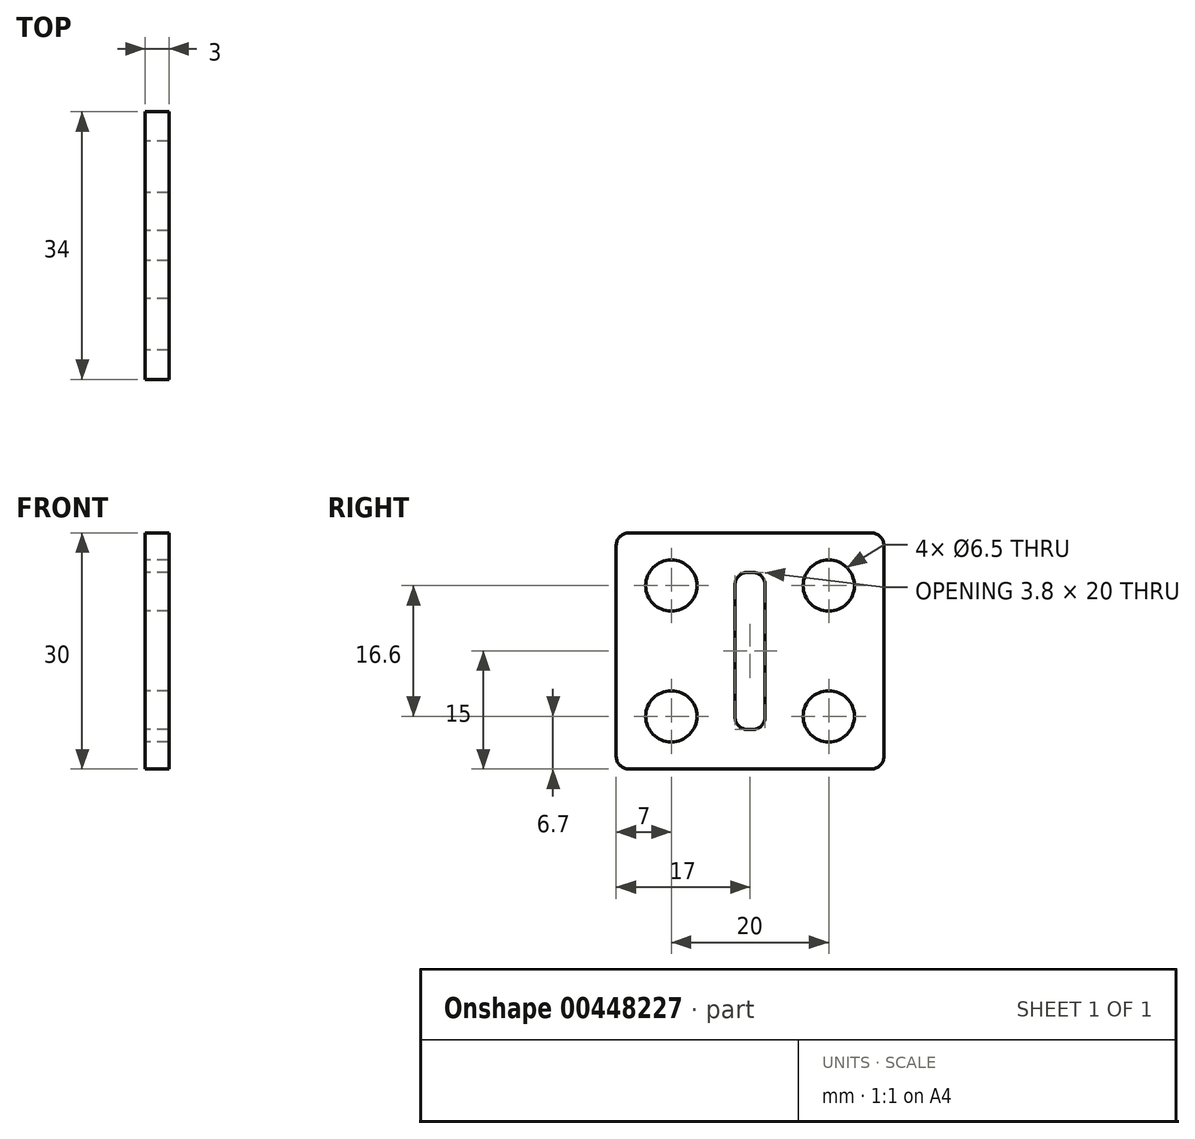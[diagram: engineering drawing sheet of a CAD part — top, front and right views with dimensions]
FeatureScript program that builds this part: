
annotation { "Feature Type Name" : "Feature", "Feature Type Description" : "" }
export const myFeature = defineFeature(function(context is Context, id is Id, definition is map)
    precondition{}
    {
        {
            var Q0;
            Q0=qCreatedBy(makeId("Right.planeOp"),FACE);
            var sketch = newSketch(context, id + "F0", { "sketchPlane" : qUnion([Q0])});
            skLineSegment(sketch, "E0.bottom", {"start": v(17, -15) * mm, "end": v(-17, -15) * mm});
            skLineSegment(sketch, "E0.top", {"start": v(17, 15) * mm, "end": v(-17, 15) * mm});
            skLineSegment(sketch, "E0.left", {"start": v(17, -15) * mm, "end": v(17, 15) * mm});
            skLineSegment(sketch, "E0.right", {"start": v(-17, -15) * mm, "end": v(-17, 15) * mm});
            skPoint(sketch, "E0.middle", {"position": v(0, 0) * mm});
            skLineSegment(sketch, "E1.bottom", {"start": v(1.9, -10) * mm, "end": v(-1.9, -10) * mm});
            skLineSegment(sketch, "E1.top", {"start": v(1.9, 10) * mm, "end": v(-1.9, 10) * mm});
            skLineSegment(sketch, "E1.left", {"start": v(1.9, -10) * mm, "end": v(1.9, 10) * mm});
            skLineSegment(sketch, "E1.right", {"start": v(-1.9, -10) * mm, "end": v(-1.9, 10) * mm});
            skLineSegment(sketch, "E2", {"start": v(10, 15) * mm, "end": v(10, -15) * mm, "construction": true});
            skLineSegment(sketch, "E3", {"start": v(-10, 15) * mm, "end": v(-10, -15) * mm, "construction": true});
            skLineSegment(sketch, "E4", {"start": v(17, 8.3) * mm, "end": v(-17, 8.3) * mm, "construction": true});
            skLineSegment(sketch, "E5", {"start": v(17, -8.3) * mm, "end": v(-17, -8.3) * mm, "construction": true});
            skPoint(sketch, "E6", {"position": v(10, 8.3) * mm});
            skPoint(sketch, "E7", {"position": v(-10, 8.3) * mm});
            skPoint(sketch, "E8", {"position": v(-10, -8.3) * mm});
            skPoint(sketch, "E9", {"position": v(10, -8.3) * mm});
            skSolve(sketch);
        }
        {
            var Q0;
            Q0=makeQuery(id+"F0.imprint","IMPRINT",FACE,{"disambiguationData":[TD([[makeQuery(id+"F0.imprint","IMPRINT",EDGE,{"derivedFrom":sQuery(id+"F0.wireOp",EDGE,"E0.bottom")}),-1.0]])]});
            extrude(context, id + "F1", {"entities" : qUnion([Q0]), "depth" : 3 * mm, "offsetDistance" : 25 * mm});
        }
        {
            var Q0;
            Q0=makeQuery(id+"F1.opExtrude","SWEPT_EDGE",EDGE,{"disambiguationData":[OSD([sQuery(id+"F0.wireOp",EDGE,"AEXB3O9J-t11H-Sehj-6pxe-2tEOLs6rYygq.top"),sQuery(id+"F0.wireOp",EDGE,"AEXB3O9J-t11H-Sehj-6pxe-2tEOLs6rYygq.right")])]});
            var Q1;
            Q1=makeQuery(id+"F1.opExtrude","SWEPT_EDGE",EDGE,{"disambiguationData":[OSD([sQuery(id+"F0.wireOp",EDGE,"AEXB3O9J-t11H-Sehj-6pxe-2tEOLs6rYygq.top"),sQuery(id+"F0.wireOp",EDGE,"AEXB3O9J-t11H-Sehj-6pxe-2tEOLs6rYygq.left")])]});
            var Q2;
            Q2=makeQuery(id+"F1.opExtrude","SWEPT_EDGE",EDGE,{"disambiguationData":[OSD([sQuery(id+"F0.wireOp",EDGE,"E1.top"),sQuery(id+"F0.wireOp",EDGE,"E1.right")])]});
            var Q3;
            Q3=makeQuery(id+"F1.opExtrude","SWEPT_EDGE",EDGE,{"disambiguationData":[OSD([sQuery(id+"F0.wireOp",EDGE,"E1.top"),sQuery(id+"F0.wireOp",EDGE,"E1.left")])]});
            var Q4;
            Q4=makeQuery(id+"F1.opExtrude","SWEPT_EDGE",EDGE,{"disambiguationData":[OSD([sQuery(id+"F0.wireOp",EDGE,"1eccf574-d479-46f1-8f8d-4602f6f3811f2.MirrorCS"),sQuery(id+"F0.wireOp",EDGE,"1eccf574-d479-46f1-8f8d-4602f6f3811f3.MirrorCS")])]});
            var Q5;
            Q5=makeQuery(id+"F1.opExtrude","SWEPT_EDGE",EDGE,{"disambiguationData":[OSD([sQuery(id+"F0.wireOp",EDGE,"1eccf574-d479-46f1-8f8d-4602f6f3811f1.MirrorCS"),sQuery(id+"F0.wireOp",EDGE,"1eccf574-d479-46f1-8f8d-4602f6f3811f3.MirrorCS")])]});
            var Q6;
            Q6=makeQuery(id+"F1.opExtrude","SWEPT_EDGE",EDGE,{"disambiguationData":[OSD([sQuery(id+"F0.wireOp",EDGE,"AEXB3O9J-t11H-Sehj-6pxe-2tEOLs6rYygq.bottom"),sQuery(id+"F0.wireOp",EDGE,"AEXB3O9J-t11H-Sehj-6pxe-2tEOLs6rYygq.right")])]});
            var Q7;
            Q7=makeQuery(id+"F1.opExtrude","SWEPT_EDGE",EDGE,{"disambiguationData":[OSD([sQuery(id+"F0.wireOp",EDGE,"AEXB3O9J-t11H-Sehj-6pxe-2tEOLs6rYygq.bottom"),sQuery(id+"F0.wireOp",EDGE,"AEXB3O9J-t11H-Sehj-6pxe-2tEOLs6rYygq.left")])]});
            var Q8;
            Q8=makeQuery(id+"F1.opExtrude","SWEPT_EDGE",EDGE,{"disambiguationData":[OSD([sQuery(id+"F0.wireOp",EDGE,"E1.bottom"),sQuery(id+"F0.wireOp",EDGE,"E1.right")])]});
            var Q9;
            Q9=makeQuery(id+"F1.opExtrude","SWEPT_EDGE",EDGE,{"disambiguationData":[OSD([sQuery(id+"F0.wireOp",EDGE,"E1.bottom"),sQuery(id+"F0.wireOp",EDGE,"E1.left")])]});
            var Q10;
            Q10=makeQuery(id+"F1.opExtrude","SWEPT_EDGE",EDGE,{"disambiguationData":[OSD([sQuery(id+"F0.wireOp",EDGE,"1eccf574-d479-46f1-8f8d-4602f6f3811f2.MirrorCS"),sQuery(id+"F0.wireOp",EDGE,"1eccf574-d479-46f1-8f8d-4602f6f3811f4.MirrorCS")])]});
            var Q11;
            Q11=makeQuery(id+"F1.opExtrude","SWEPT_EDGE",EDGE,{"disambiguationData":[OSD([sQuery(id+"F0.wireOp",EDGE,"1eccf574-d479-46f1-8f8d-4602f6f3811f1.MirrorCS"),sQuery(id+"F0.wireOp",EDGE,"1eccf574-d479-46f1-8f8d-4602f6f3811f4.MirrorCS")])]});
            var Q12;
            Q12=makeQuery(id+"F1.opExtrude","SWEPT_EDGE",EDGE,{"disambiguationData":[OSD([sQuery(id+"F0.wireOp",EDGE,"E0.top"),sQuery(id+"F0.wireOp",EDGE,"E0.right")])]});
            var Q13;
            Q13=makeQuery(id+"F1.opExtrude","SWEPT_EDGE",EDGE,{"disambiguationData":[OSD([sQuery(id+"F0.wireOp",EDGE,"E0.top"),sQuery(id+"F0.wireOp",EDGE,"E0.left")])]});
            var Q14;
            Q14=makeQuery(id+"F1.opExtrude","SWEPT_EDGE",EDGE,{"disambiguationData":[OSD([sQuery(id+"F0.wireOp",EDGE,"E0.bottom"),sQuery(id+"F0.wireOp",EDGE,"E0.left")])]});
            var Q15;
            Q15=makeQuery(id+"F1.opExtrude","SWEPT_EDGE",EDGE,{"disambiguationData":[OSD([sQuery(id+"F0.wireOp",EDGE,"E0.bottom"),sQuery(id+"F0.wireOp",EDGE,"E0.right")])]});
            fillet(context, id + "F2", {"entities" : qUnion([Q0, Q1, Q2, Q3, Q4, Q5, Q6, Q7, Q8, Q9, Q10, Q11, Q12, Q13, Q14, Q15]), "radius" : 1.6 * mm, "tangentPropagation" : true, "allowEdgeOverflow" : false});
        }
        {
            var Q0;
            Q0=sQuery(id+"F0.wireOp",VERTEX,"E6");
            var Q1;
            Q1=sQuery(id+"F0.wireOp",VERTEX,"E7");
            var Q2;
            Q2=sQuery(id+"F0.wireOp",VERTEX,"E8");
            var Q3;
            Q3=sQuery(id+"F0.wireOp",VERTEX,"E9");
            var Q4;
            Q4=makeQuery(id+"F1.opExtrude","SWEPT_BODY",BODY,{"disambiguationData":[OSD([sQuery(id+"F0.wireOp",EDGE,"E0.bottom"),sQuery(id+"F0.wireOp",EDGE,"E0.top"),sQuery(id+"F0.wireOp",EDGE,"E0.left"),sQuery(id+"F0.wireOp",EDGE,"E0.right"),sQuery(id+"F0.wireOp",EDGE,"E1.bottom"),sQuery(id+"F0.wireOp",EDGE,"E1.top"),sQuery(id+"F0.wireOp",EDGE,"E1.left"),sQuery(id+"F0.wireOp",EDGE,"E1.right")])]});
            hole(context, id + "F3", {"style" : HoleStyle.C_BORE, "endStyle" : HoleEndStyle.THROUGH, "oppositeDirection" : true, "standardTappedOrClearance" : lookupTablePath({ "standard" : "ISO", "fit" : "Normal", "size" : "M3", "type" : "Clearance" }), "standardBlindInLast" : lookupTablePath({ "fit" : "Standard", "standard" : "ISO", "size" : "M3", "type" : "Clearance" }), "holeDiameter" : 3.3 * mm, "cBoreDiameter" : 6.5 * mm, "cBoreDepth" : 3 * mm, "majorDiameter" : 5 * mm, "isTappedThrough" : true, "tappedDepth" : 12 * mm, "tapClearance" : 3, "locations" : qUnion([Q0, Q1, Q2, Q3]), "scope" : qUnion([Q4])});
        }
    });
